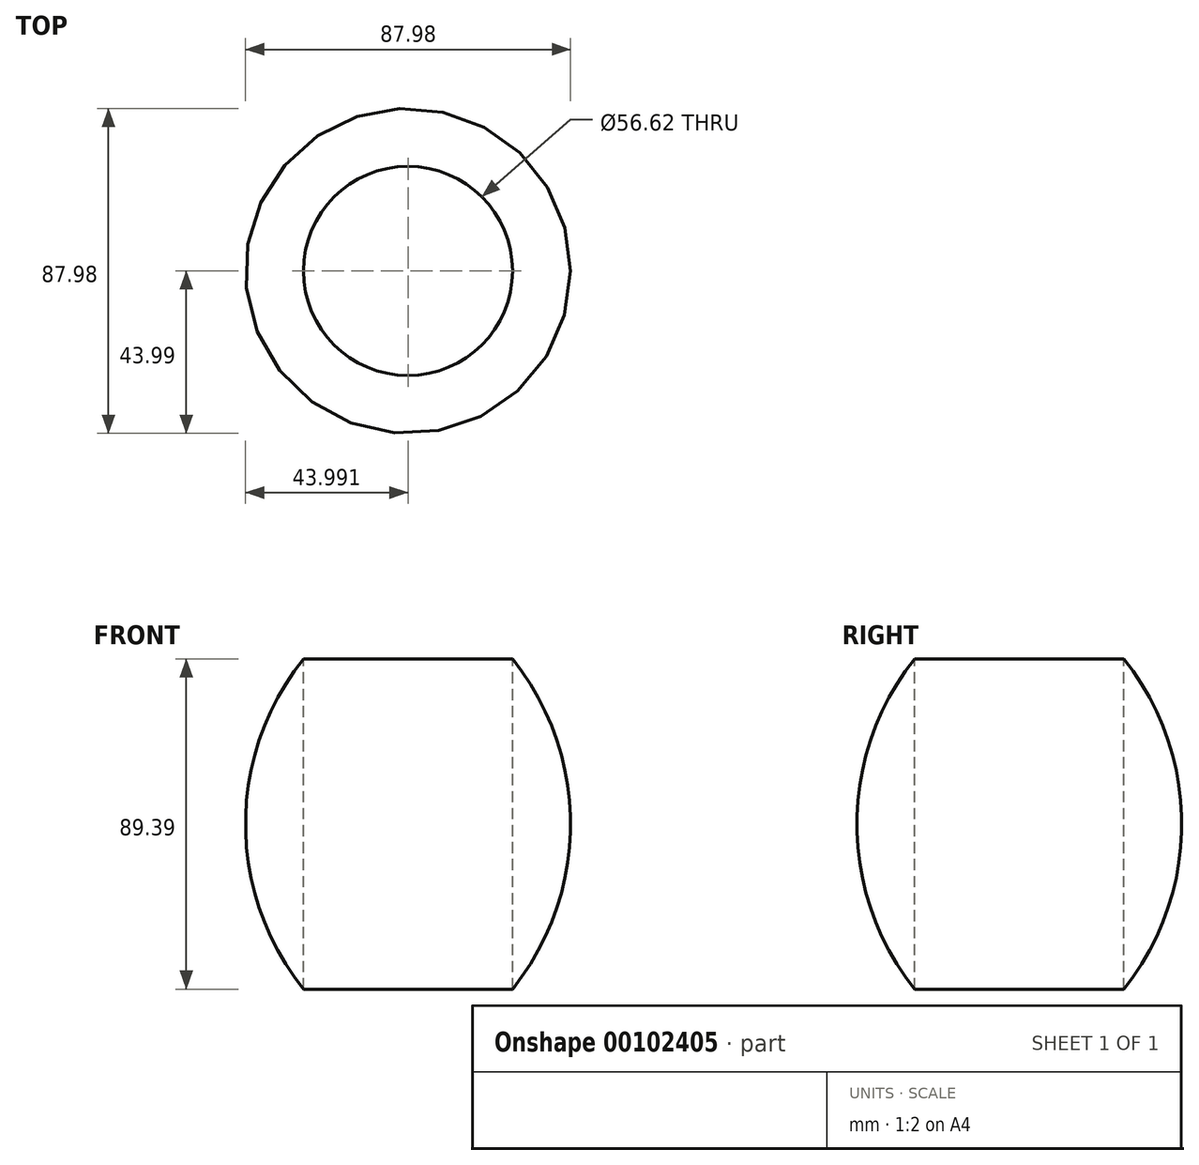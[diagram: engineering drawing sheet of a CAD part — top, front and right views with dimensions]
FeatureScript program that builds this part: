
annotation { "Feature Type Name" : "Feature", "Feature Type Description" : "" }
export const myFeature = defineFeature(function(context is Context, id is Id, definition is map)
    precondition{}
    {
        {
            var Q0;
            Q0=qCreatedBy(makeId("Front.planeOp"),FACE);
            var sketch = newSketch(context, id + "F0", { "sketchPlane" : qUnion([Q0])});
            skLineSegment(sketch, "E0", {"start": v(-43.2, 54.08) * mm, "end": v(-43.2, -35.31) * mm});
            skArc(sketch, "E1", {"start": v(-43.2, 54.08) * mm, "mid": v(-58.89, 9.39) * mm, "end": v(-43.2, -35.31) * mm});
            skLineSegment(sketch, "E2", {"start": v(-14.9, 64.81) * mm, "end": v(-14.9, -47.83) * mm});
            skSolve(sketch);
        }
        {
            var Q0;
            Q0=makeQuery(id+"F0.imprint","IMPRINT",FACE,{"disambiguationData":[TD([[makeQuery(id+"F0.imprint","IMPRINT",EDGE,{"derivedFrom":sQuery(id+"F0.wireOp",EDGE,"E0")}),-1.0]])]});
            var Q1;
            Q1=sQuery(id+"F0.wireOp",EDGE,"E2");
            revolve(context, id + "F1", {"entities" : qUnion([Q0]), "axis" : qUnion([Q1]), "revolveType" : RevolveType.FULL});
        }
    });
